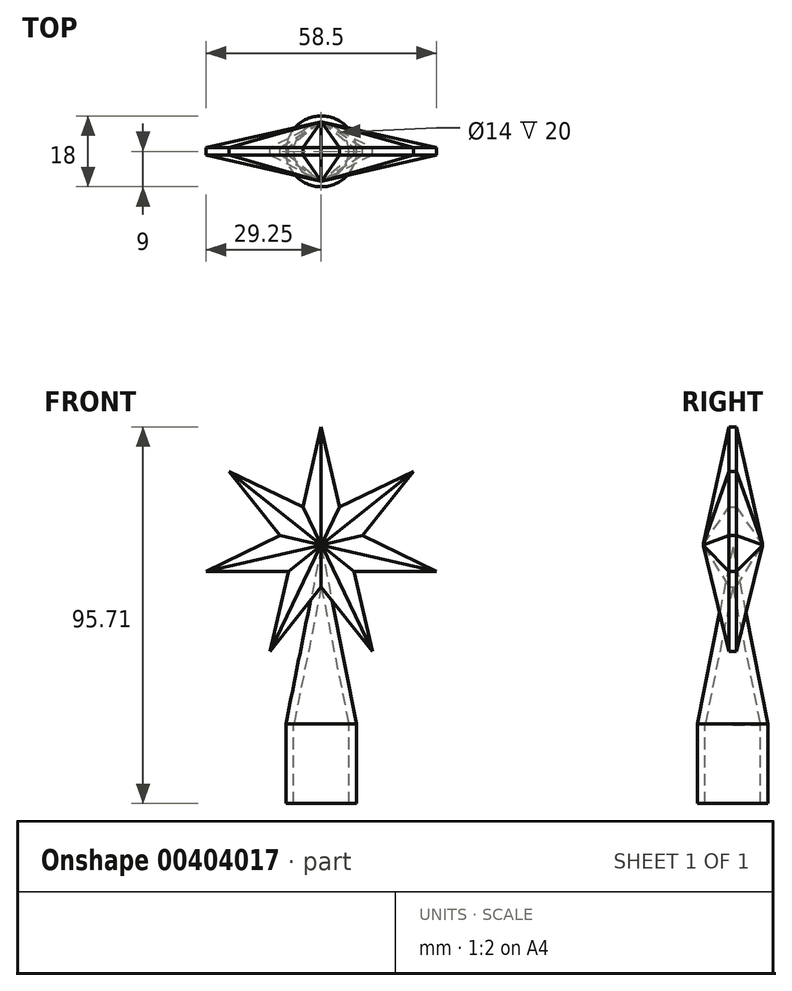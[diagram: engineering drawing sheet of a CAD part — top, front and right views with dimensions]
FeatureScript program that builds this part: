
annotation { "Feature Type Name" : "Feature", "Feature Type Description" : "" }
export const myFeature = defineFeature(function(context is Context, id is Id, definition is map)
    precondition{}
    {
        {
            var Q0;
            Q0=qCreatedBy(makeId("Front.planeOp"),FACE);
            var sketch = newSketch(context, id + "F0", { "sketchPlane" : qUnion([Q0])});
            skLineSegment(sketch, "E0", {"start": v(0, 0) * mm, "end": v(0, 30) * mm, "construction": true});
            skCircle(sketch, "E1.cCircle", {"center": v(0, 0) * mm, "radius": 30 * mm, "construction": true});
            skLineSegment(sketch, "E1.0", {"start": v(0, 30) * mm, "end": v(23.45, 18.7) * mm, "construction": true});
            skLineSegment(sketch, "E1.1", {"start": v(23.45, 18.7) * mm, "end": v(29.25, -6.68) * mm, "construction": true});
            skLineSegment(sketch, "E1.2", {"start": v(29.25, -6.68) * mm, "end": v(13.02, -27.03) * mm, "construction": true});
            skLineSegment(sketch, "E1.3", {"start": v(13.02, -27.03) * mm, "end": v(-13.02, -27.03) * mm, "construction": true});
            skLineSegment(sketch, "E1.4", {"start": v(-13.02, -27.03) * mm, "end": v(-29.25, -6.68) * mm, "construction": true});
            skLineSegment(sketch, "E1.5", {"start": v(-29.25, -6.68) * mm, "end": v(-23.45, 18.7) * mm, "construction": true});
            skLineSegment(sketch, "E1.6", {"start": v(-23.45, 18.7) * mm, "end": v(0, 30) * mm, "construction": true});
            skLineSegment(sketch, "E2", {"start": v(-13.02, -27.03) * mm, "end": v(0, 30) * mm});
            skLineSegment(sketch, "E3", {"start": v(0, 30) * mm, "end": v(13.02, -27.03) * mm});
            skLineSegment(sketch, "E4", {"start": v(13.02, -27.03) * mm, "end": v(-23.45, 18.7) * mm});
            skLineSegment(sketch, "E5", {"start": v(-23.45, 18.7) * mm, "end": v(29.25, -6.68) * mm});
            skLineSegment(sketch, "E6", {"start": v(29.25, -6.68) * mm, "end": v(-29.25, -6.68) * mm});
            skLineSegment(sketch, "E7", {"start": v(-29.25, -6.68) * mm, "end": v(23.45, 18.7) * mm});
            skPoint(sketch, "E8", {"position": v(0, -10.7) * mm});
            skLineSegment(sketch, "E9", {"start": v(0, -10.7) * mm, "end": v(0, -45.7) * mm, "construction": true});
            skLineSegment(sketch, "E10", {"start": v(0, -45.7) * mm, "end": v(-7, -45.7) * mm, "construction": true});
            skLineSegment(sketch, "E11", {"start": v(-7, -45.7) * mm, "end": v(0, -10.7) * mm});
            skLineSegment(sketch, "E12", {"start": v(-7, -45.7) * mm, "end": v(-7, -65.7) * mm});
            skLineSegment(sketch, "E13", {"start": v(-13.02, -27.03) * mm, "end": v(23.45, 18.7) * mm});
            skLineSegment(sketch, "E14.0", {"start": v(-9, -45.5) * mm, "end": v(-1.96, -10.33) * mm});
            skLineSegment(sketch, "E14.1", {"start": v(-9, -45.5) * mm, "end": v(-9, -65.7) * mm});
            skLineSegment(sketch, "E15", {"start": v(-9, -65.7) * mm, "end": v(-7, -65.7) * mm});
            skLineSegment(sketch, "E16", {"start": v(-1.96, -10.33) * mm, "end": v(0, -0.5) * mm});
            skLineSegment(sketch, "E17", {"start": v(0, -10.7) * mm, "end": v(0, 0) * mm, "construction": true});
            skLineSegment(sketch, "E18", {"start": v(0, -10.7) * mm, "end": v(0, -0.5) * mm});
            skSolve(sketch);
        }
        {
            var Q0;
            {var subQ0=sQuery(id+"F0.wireOp",EDGE,"E18");var subQ5=sQuery(id+"F0.wireOp",EDGE,"E6");var subQ7=makeQuery(id+"F0.imprint","INTERSECT",VERTEX,{"derivedFrom":[subQ5,subQ0]});Q0=makeQuery(id+"F0.imprint","IMPRINT",FACE,{"disambiguationData":[TD([[makeQuery(id+"F0.imprint","IMPRINT",EDGE,{"disambiguationData":[TD([[subQ7,-1.0]])],"derivedFrom":subQ5}),1.0]])]});}
            var Q1;
            {var subQ0=sQuery(id+"F0.wireOp",EDGE,"E13");var subQ1=sQuery(id+"F0.wireOp",EDGE,"E6");var subQ2=makeQuery(id+"F0.imprint","INTERSECT",VERTEX,{"derivedFrom":[subQ1,subQ0]});Q1=makeQuery(id+"F0.imprint","IMPRINT",FACE,{"disambiguationData":[TD([[makeQuery(id+"F0.imprint","IMPRINT",EDGE,{"disambiguationData":[TD([[subQ2,-1.0]])],"derivedFrom":subQ1}),1.0]])]});}
            var Q2;
            {var subQ3=sQuery(id+"F0.wireOp",EDGE,"E16");var subQ5=sQuery(id+"F0.wireOp",EDGE,"E14.0");var subQ7=makeQuery(id+"F0.imprint","INTERSECT",VERTEX,{"derivedFrom":[subQ5,subQ3]});Q2=makeQuery(id+"F0.imprint","IMPRINT",FACE,{"disambiguationData":[TD([[makeQuery(id+"F0.imprint","IMPRINT",EDGE,{"disambiguationData":[TD([[subQ7,1.0]])],"derivedFrom":subQ5}),-1.0]])]});}
            var Q3;
            {var subQ0=sQuery(id+"F0.wireOp",EDGE,"E16");var subQ1=sQuery(id+"F0.wireOp",EDGE,"E4");var subQ2=makeQuery(id+"F0.imprint","INTERSECT",VERTEX,{"derivedFrom":[subQ1,subQ0]});Q3=makeQuery(id+"F0.imprint","IMPRINT",FACE,{"disambiguationData":[TD([[makeQuery(id+"F0.imprint","IMPRINT",EDGE,{"disambiguationData":[TD([[subQ2,-1.0]])],"derivedFrom":subQ1}),-1.0]])]});}
            var Q4;
            {var subQ1=sQuery(id+"F0.wireOp",EDGE,"E2");var subQ9=sQuery(id+"F0.wireOp",EDGE,"E13");var subQ10=makeQuery(id+"F0.imprint","INTERSECT",VERTEX,{"derivedFrom":[subQ1,subQ9]});Q4=makeQuery(id+"F0.imprint","IMPRINT",FACE,{"disambiguationData":[TD([[makeQuery(id+"F0.imprint","IMPRINT",EDGE,{"disambiguationData":[TD([[subQ10,-1.0]])],"derivedFrom":subQ1}),-1.0]])]});}
            var Q5;
            {var subQ0=sQuery(id+"F0.wireOp",EDGE,"E4");var subQ1=sQuery(id+"F0.wireOp",EDGE,"E3");var subQ2=makeQuery(id+"F0.imprint","INTERSECT",VERTEX,{"derivedFrom":[subQ1,subQ0]});Q5=makeQuery(id+"F0.imprint","IMPRINT",FACE,{"disambiguationData":[TD([[makeQuery(id+"F0.imprint","IMPRINT",EDGE,{"disambiguationData":[TD([[subQ2,1.0]])],"derivedFrom":subQ1}),-1.0]])]});}
            var Q6;
            {var subQ0=sQuery(id+"F0.wireOp",EDGE,"E6");var subQ1=sQuery(id+"F0.wireOp",EDGE,"E3");var subQ2=makeQuery(id+"F0.imprint","INTERSECT",VERTEX,{"derivedFrom":[subQ1,subQ0]});Q6=makeQuery(id+"F0.imprint","IMPRINT",FACE,{"disambiguationData":[TD([[makeQuery(id+"F0.imprint","IMPRINT",EDGE,{"disambiguationData":[TD([[subQ2,1.0]])],"derivedFrom":subQ1}),-1.0]])]});}
            var Q7;
            {var subQ0=sQuery(id+"F0.wireOp",EDGE,"E6");var subQ1=sQuery(id+"F0.wireOp",EDGE,"E2");var subQ2=makeQuery(id+"F0.imprint","INTERSECT",VERTEX,{"derivedFrom":[subQ1,subQ0]});Q7=makeQuery(id+"F0.imprint","IMPRINT",FACE,{"disambiguationData":[TD([[makeQuery(id+"F0.imprint","IMPRINT",EDGE,{"disambiguationData":[TD([[subQ2,-1.0]])],"derivedFrom":subQ1}),-1.0]])]});}
            var Q8;
            {var subQ0=sQuery(id+"F0.wireOp",EDGE,"E6");var subQ1=sQuery(id+"F0.wireOp",EDGE,"E2");var subQ2=makeQuery(id+"F0.imprint","INTERSECT",VERTEX,{"derivedFrom":[subQ1,subQ0]});Q8=makeQuery(id+"F0.imprint","IMPRINT",FACE,{"disambiguationData":[TD([[makeQuery(id+"F0.imprint","IMPRINT",EDGE,{"disambiguationData":[TD([[subQ2,-1.0]])],"derivedFrom":subQ1}),1.0]])]});}
            var Q9;
            {var subQ0=sQuery(id+"F0.wireOp",EDGE,"E4");var subQ1=sQuery(id+"F0.wireOp",EDGE,"E2");var subQ2=makeQuery(id+"F0.imprint","INTERSECT",VERTEX,{"derivedFrom":[subQ1,subQ0]});Q9=makeQuery(id+"F0.imprint","IMPRINT",FACE,{"disambiguationData":[TD([[makeQuery(id+"F0.imprint","IMPRINT",EDGE,{"disambiguationData":[TD([[subQ2,-1.0]])],"derivedFrom":subQ1}),1.0]])]});}
            var Q10;
            {var subQ0=sQuery(id+"F0.wireOp",EDGE,"E5");var subQ1=sQuery(id+"F0.wireOp",EDGE,"E2");var subQ2=makeQuery(id+"F0.imprint","INTERSECT",VERTEX,{"derivedFrom":[subQ1,subQ0]});Q10=makeQuery(id+"F0.imprint","IMPRINT",FACE,{"disambiguationData":[TD([[makeQuery(id+"F0.imprint","IMPRINT",EDGE,{"disambiguationData":[TD([[subQ2,1.0]])],"derivedFrom":subQ1}),1.0]])]});}
            var Q11;
            {var subQ0=sQuery(id+"F0.wireOp",EDGE,"E5");var subQ1=sQuery(id+"F0.wireOp",EDGE,"E2");var subQ2=makeQuery(id+"F0.imprint","INTERSECT",VERTEX,{"derivedFrom":[subQ1,subQ0]});Q11=makeQuery(id+"F0.imprint","IMPRINT",FACE,{"disambiguationData":[TD([[makeQuery(id+"F0.imprint","IMPRINT",EDGE,{"disambiguationData":[TD([[subQ2,1.0]])],"derivedFrom":subQ1}),-1.0]])]});}
            var Q12;
            {var subQ0=sQuery(id+"F0.wireOp",EDGE,"E3");var subQ1=sQuery(id+"F0.wireOp",EDGE,"E2");var subQ2=makeQuery(id+"F0.imprint","INTERSECT",VERTEX,{"derivedFrom":[subQ1,subQ0]});Q12=makeQuery(id+"F0.imprint","IMPRINT",FACE,{"disambiguationData":[TD([[makeQuery(id+"F0.imprint","IMPRINT",EDGE,{"disambiguationData":[TD([[subQ2,1.0]])],"derivedFrom":subQ1}),-1.0]])]});}
            var Q13;
            {var subQ0=sQuery(id+"F0.wireOp",EDGE,"E7");var subQ1=sQuery(id+"F0.wireOp",EDGE,"E3");var subQ2=makeQuery(id+"F0.imprint","INTERSECT",VERTEX,{"derivedFrom":[subQ1,subQ0]});Q13=makeQuery(id+"F0.imprint","IMPRINT",FACE,{"disambiguationData":[TD([[makeQuery(id+"F0.imprint","IMPRINT",EDGE,{"disambiguationData":[TD([[subQ2,-1.0]])],"derivedFrom":subQ1}),-1.0]])]});}
            var Q14;
            {var subQ0=sQuery(id+"F0.wireOp",EDGE,"E7");var subQ1=sQuery(id+"F0.wireOp",EDGE,"E3");var subQ2=makeQuery(id+"F0.imprint","INTERSECT",VERTEX,{"derivedFrom":[subQ1,subQ0]});Q14=makeQuery(id+"F0.imprint","IMPRINT",FACE,{"disambiguationData":[TD([[makeQuery(id+"F0.imprint","IMPRINT",EDGE,{"disambiguationData":[TD([[subQ2,-1.0]])],"derivedFrom":subQ1}),1.0]])]});}
            var Q15;
            {var subQ0=sQuery(id+"F0.wireOp",EDGE,"E5");var subQ1=sQuery(id+"F0.wireOp",EDGE,"E3");var subQ2=makeQuery(id+"F0.imprint","INTERSECT",VERTEX,{"derivedFrom":[subQ1,subQ0]});Q15=makeQuery(id+"F0.imprint","IMPRINT",FACE,{"disambiguationData":[TD([[makeQuery(id+"F0.imprint","IMPRINT",EDGE,{"disambiguationData":[TD([[subQ2,-1.0]])],"derivedFrom":subQ1}),1.0]])]});}
            var Q16;
            {var subQ0=sQuery(id+"F0.wireOp",EDGE,"E6");var subQ1=sQuery(id+"F0.wireOp",EDGE,"E3");var subQ2=makeQuery(id+"F0.imprint","INTERSECT",VERTEX,{"derivedFrom":[subQ1,subQ0]});Q16=makeQuery(id+"F0.imprint","IMPRINT",FACE,{"disambiguationData":[TD([[makeQuery(id+"F0.imprint","IMPRINT",EDGE,{"disambiguationData":[TD([[subQ2,1.0]])],"derivedFrom":subQ1}),1.0]])]});}
            var Q17;
            {var subQ7=sQuery(id+"F0.wireOp",EDGE,"E4");var subQ8=sQuery(id+"F0.wireOp",EDGE,"E2");var subQ9=makeQuery(id+"F0.imprint","INTERSECT",VERTEX,{"derivedFrom":[subQ8,subQ7]});Q17=makeQuery(id+"F0.imprint","IMPRINT",FACE,{"disambiguationData":[TD([[makeQuery(id+"F0.imprint","IMPRINT",EDGE,{"disambiguationData":[TD([[subQ9,-1.0]])],"derivedFrom":subQ8}),-1.0]])]});}
            var Q18;
            {var subQ0=sQuery(id+"F0.wireOp",EDGE,"E18");var subQ1=sQuery(id+"F0.wireOp",EDGE,"E6");var subQ2=makeQuery(id+"F0.imprint","INTERSECT",VERTEX,{"derivedFrom":[subQ1,subQ0]});Q18=makeQuery(id+"F0.imprint","IMPRINT",FACE,{"disambiguationData":[TD([[makeQuery(id+"F0.imprint","IMPRINT",EDGE,{"disambiguationData":[TD([[subQ2,-1.0]])],"derivedFrom":subQ1}),-1.0]])]});}
            extrude(context, id + "F1", {"entities" : qUnion([Q0, Q1, Q2, Q3, Q4, Q5, Q6, Q7, Q8, Q9, Q10, Q11, Q12, Q13, Q14, Q15, Q16, Q17, Q18]), "endBound" : BoundingType.SYMMETRIC, "depth" : 15 * mm});
        }
        {
            var Q0;
            {var subQ4=sQuery(id+"F0.wireOp",EDGE,"E11");Q0=makeQuery(id+"F0.imprint","IMPRINT",FACE,{"disambiguationData":[TD([[makeQuery(id+"F0.imprint","IMPRINT",EDGE,{"derivedFrom":subQ4}),1.0]])]});}
            var Q1;
            {var subQ3=sQuery(id+"F0.wireOp",EDGE,"E16");var subQ5=sQuery(id+"F0.wireOp",EDGE,"E14.0");var subQ7=makeQuery(id+"F0.imprint","INTERSECT",VERTEX,{"derivedFrom":[subQ5,subQ3]});Q1=makeQuery(id+"F0.imprint","IMPRINT",FACE,{"disambiguationData":[TD([[makeQuery(id+"F0.imprint","IMPRINT",EDGE,{"disambiguationData":[TD([[subQ7,1.0]])],"derivedFrom":subQ5}),-1.0]])]});}
            var Q2;
            {var subQ0=sQuery(id+"F0.wireOp",EDGE,"E18");var subQ5=sQuery(id+"F0.wireOp",EDGE,"E6");var subQ7=makeQuery(id+"F0.imprint","INTERSECT",VERTEX,{"derivedFrom":[subQ5,subQ0]});Q2=makeQuery(id+"F0.imprint","IMPRINT",FACE,{"disambiguationData":[TD([[makeQuery(id+"F0.imprint","IMPRINT",EDGE,{"disambiguationData":[TD([[subQ7,-1.0]])],"derivedFrom":subQ5}),1.0]])]});}
            var Q3;
            {var subQ0=sQuery(id+"F0.wireOp",EDGE,"E18");var subQ1=sQuery(id+"F0.wireOp",EDGE,"E6");var subQ2=makeQuery(id+"F0.imprint","INTERSECT",VERTEX,{"derivedFrom":[subQ1,subQ0]});Q3=makeQuery(id+"F0.imprint","IMPRINT",FACE,{"disambiguationData":[TD([[makeQuery(id+"F0.imprint","IMPRINT",EDGE,{"disambiguationData":[TD([[subQ2,-1.0]])],"derivedFrom":subQ1}),-1.0]])]});}
            var Q4;
            Q4=sQuery(id+"F0.wireOp",EDGE,"E9");
            revolve(context, id + "F2", {"entities" : qUnion([Q0, Q1, Q2, Q3]), "axis" : qUnion([Q4]), "revolveType" : RevolveType.FULL});
        }
        {
            var Q0;
            Q0=makeQuery(id+"F1.opExtrude","CAP_FACE",FACE,{"disambiguationData":[OSD([sQuery(id+"F0.wireOp",EDGE,"E2"),sQuery(id+"F0.wireOp",EDGE,"E3"),sQuery(id+"F0.wireOp",EDGE,"E4"),sQuery(id+"F0.wireOp",EDGE,"E5"),sQuery(id+"F0.wireOp",EDGE,"E6"),sQuery(id+"F0.wireOp",EDGE,"E7"),sQuery(id+"F0.wireOp",EDGE,"E13")])],"isStart":false});
            var Q1;
            Q1=makeQuery(id+"F1.opExtrude","CAP_FACE",FACE,{"disambiguationData":[OSD([sQuery(id+"F0.wireOp",EDGE,"E2"),sQuery(id+"F0.wireOp",EDGE,"E3"),sQuery(id+"F0.wireOp",EDGE,"E4"),sQuery(id+"F0.wireOp",EDGE,"E5"),sQuery(id+"F0.wireOp",EDGE,"E6"),sQuery(id+"F0.wireOp",EDGE,"E7"),sQuery(id+"F0.wireOp",EDGE,"E13")])],"isStart":true});
            chamfer(context, id + "F3", {"entities" : qUnion([Q0, Q1]), "width" : 6.6 * mm, "tangentPropagation" : true});
        }
    });
